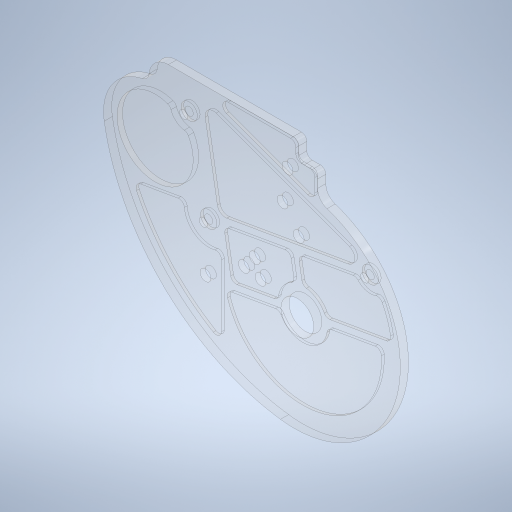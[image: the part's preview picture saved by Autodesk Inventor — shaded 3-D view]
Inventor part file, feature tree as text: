
AUTODESK INVENTOR PART (.ipt)
format: ipt  version: 2023.1 (Build 271208000, 208)  size: 540,160 bytes
history: native  units: mm
features: extrude x3, sketch x2
ambient origin geometry x8: Origin, YZ Plane, XZ Plane, XY Plane, X Axis, Y Axis, Z Axis, Center Point
bodies: Solid2 (feature_tree)
feature tree (5):
  sketch  "Sketch6"  dims[d185=3.0mm d186=0.0mm]
  extrude  "Extrusion4"  Depth=1.0mm TaperAngle=0.0deg
  sketch  "Sketch10"  dims[d196=4.0mm d197=60.0mm d198=76.0mm d199=39.0mm d200=5.0mm d201=6.0mm d202=6.0mm d203=25.0mm d204=6.0mm d205=37.0mm d206=13.0mm d207=1.0mm d208=3.14mm d209=48.591233mm d210=42.887988mm d211=24.0mm d212=3.0mm d213=3.0mm d214=12.05mm d215=3.0mm d216=3.0mm d217=3.0mm d218=3.0mm d219=3.0mm d220=3.0mm d221=3.0mm d222=30.0deg d223=90.0deg d224=2.0mm d225=2.0mm d226=3.0mm d227=2.0mm d228=2.0mm d229=2.0mm d230=3.0mm d231=1.5mm d232=1.5mm d233=2.0mm d234=2.0mm d235=2.0mm d236=3.0mm d237=1.5mm d238=3.0mm d239=2.0mm d240=1.5mm d241=2.0mm d242=2.0mm d243=2.0mm d244=2.0mm d245=3.0mm d246=1.5mm d247=1.5mm d248=2.0mm d249=2.0mm d250=20.0mm d251=2.0mm d252=2.0mm d253=2.0mm d254=4.0mm d255=2.0mm d256=2.0mm d257=2.0mm d258=3.0mm d259=3.0mm d260=2.0mm d261=2.0mm d262=3.0mm d263=3.0mm d264=2.0mm d265=3.0mm d266=46.0mm d267=55.0mm d268=5.0mm d269=3.0mm d270=2.0mm d271=3.0mm d272=2.0mm d273=2.0mm d274=2.0mm d275=3.0mm d276=2.0mm d277=2.0mm d278=3.0mm d279=1.0mm d280=0.0mm d281=14.05mm d284=2.0mm d285=0.0mm d287=4.0mm d288=4.0mm d289=4.0mm d290=4.0mm d291=4.0mm d292=4.0mm d293=4.0mm d25=0.5mm d26=0.872665mm d27=0.5mm d28=0.872665mm d56=0.5mm d57=0.872665mm d58=0.5mm d59=0.872665mm d282=0.5mm d283=0.872665mm]
  extrude  "Extrusion9"  Depth=4.0mm
  extrude  "Extrusion11"  Depth=2.0mm TaperAngle=0.0deg
